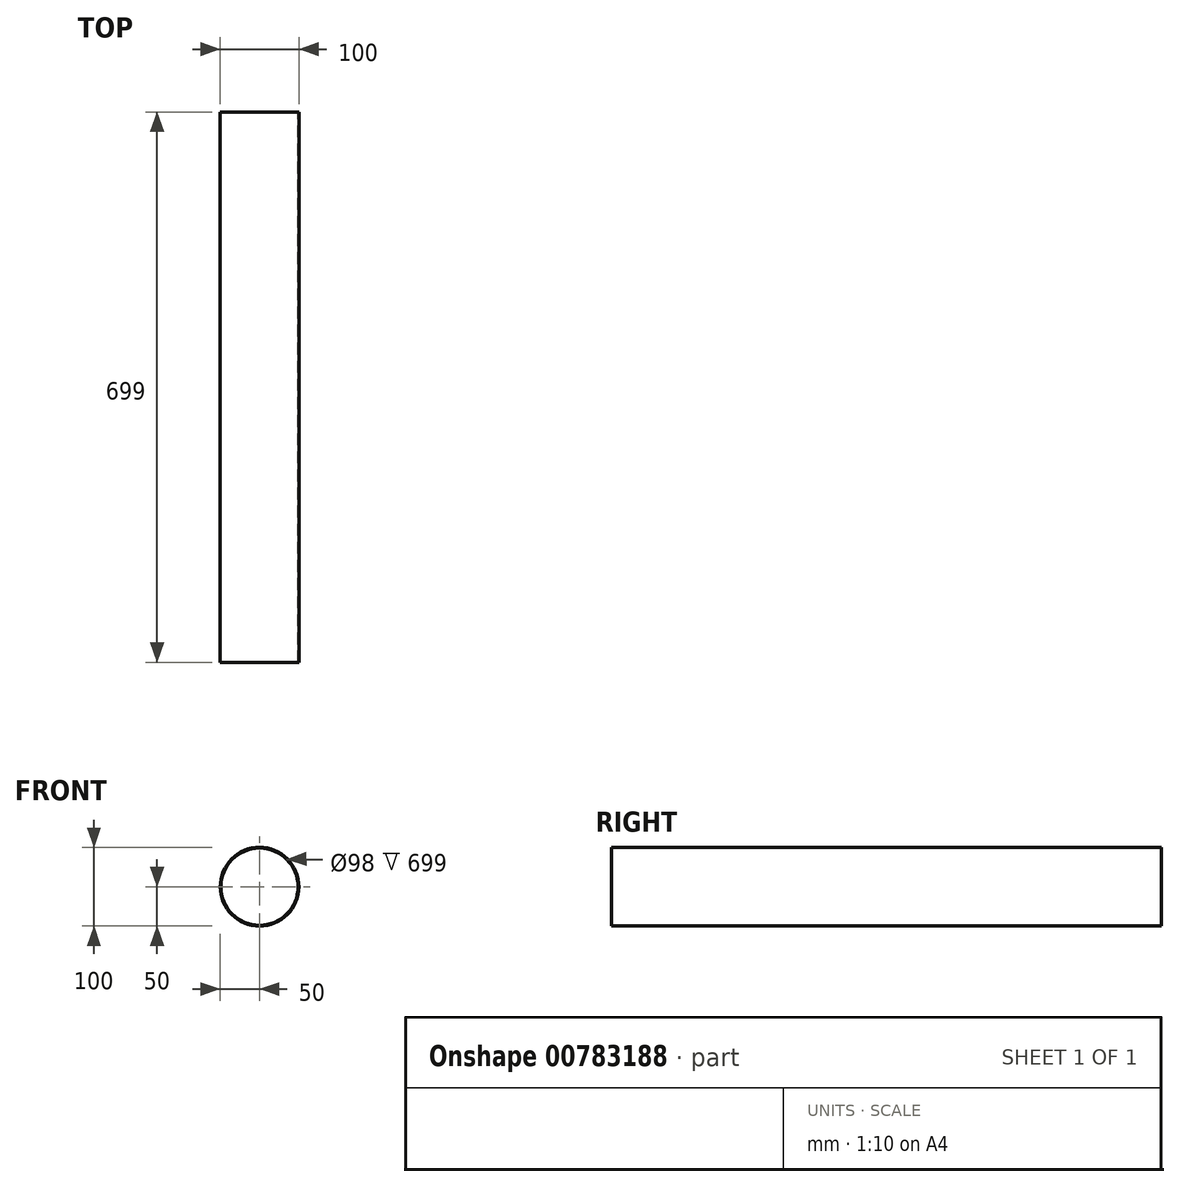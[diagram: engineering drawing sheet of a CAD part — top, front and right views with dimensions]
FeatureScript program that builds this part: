
annotation { "Feature Type Name" : "Feature", "Feature Type Description" : "" }
export const myFeature = defineFeature(function(context is Context, id is Id, definition is map)
    precondition{}
    {
        {
            var Q0;
            Q0=qCreatedBy(makeId("Front.planeOp"),FACE);
            var sketch = newSketch(context, id + "F0", { "sketchPlane" : qUnion([Q0])});
            skCircle(sketch, "E0", {"center": v(0, 0) * mm, "radius": 50 * mm});
            skCircle(sketch, "E1", {"center": v(0, 0) * mm, "radius": 49 * mm});
            skSolve(sketch);
        }
        {
            var Q0;
            Q0=qSketchRegion(id+"F0",true);
            extrude(context, id + "F1", {"entities" : qUnion([Q0]), "depth" : 699 * mm, "offsetDistance" : 25 * mm});
        }
    });
